# Revit family: IS_Connect_E7912_BIM_FR
name_source: partatom
category: Plumbing Fixtures
revit_build: Autodesk Revit 2017 (Build: 20160225_1515(x64)
units: mm (PartAtom-declared; Revit-internal decimal feet)

## family parameters
Always vertical = No
Cut with Voids When Loaded = No
OmniClass Number = 23.45.05.14.14
OmniClass Title = Sinks/Lavatories
Part Type = Normal
Room Calculation Point = No
Round Connector Dimension = Use Diameter
Shared = No
Work Plane-Based = No

## types (1)
- E791201 - CONNECT LAVE-MAINS ARC 35x26 1T GCHE BLC
    Accessoires = www.idealstandard.be
    Auteur = Ideal Standard
    BOSUseNativeGeometries = 1
    Bim-NomDuProjet = ISI_IdealStandard_PedestalWashBasins_CONNECT_E791201
    Caractéristiques = CONNECT ARC H/R BSN 35X26 WHITEIP 1LT
    CodeBarre = 5017830389422
    ConseilsDInstallation = www.idealstandard.be
    Cost = 0 $
    Couleur = Blanc
    CoûtDeRemplacement = 0
    DateDeCréation = 2018_08_15
    Description = CONNECT Lave-mains 35 x 26 cm
 version gauche
    DiamètreÉvacuation = 0
    Dimensions = 153 x 350 x 262mm
    Espace = Interne
    Finition = Blanc
    Forme = Complexe
    Hauteur = 153 mm
    IfcExportAs = WASHBASIN
    IfcExportType = IfcSanitaryTerminalType
    InformationsProduit = www.idealstandard.be
    Largeur = 350 mm
    LienUtile = www.idealstandard.be
    Longueur = 262 mm
    Manufacturer = www.idealstandard.be
    Marque = Ideal Standard
    Matériel = Ceramics
    Model = E791201
    Profondeur = 0 mm  [stored 0 ft]
    Raccordement = Plomberie
    Révision = 1
    TypeDeLavabo = Hand Rinse Basin
    URL = www.idealstandard.be
    Uniclass2015Code = Pr_40_20_87_98
    Uniclass2015Title = Washbasin taps
    Uniclass2015Version = Products v1.1
    UnitéDeMesure = Millimètres
    UnitéDeTemps = An
    UnitéMonétaire = €
    UrlDuFabricant = www.idealstandard.be
    Version = 1

note: [stored X ft] marks values corroborated as IEEE doubles in the binary element streams (Revit-internal decimal feet)

## geometry (parser evidence)
native form markers: Sweep x4
no freeform markers — native parametric forms only
